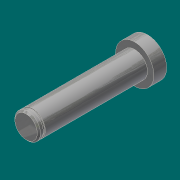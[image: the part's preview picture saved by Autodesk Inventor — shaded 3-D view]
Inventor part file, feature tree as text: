
AUTODESK INVENTOR PART (.ipt)
format: ipt  version: 2017 (Build 210142000, 142)  size: 109,568 bytes
history: native  units: in
note: dims shown in document units (in); Inventor stores cm internally (conversion verified against a paired STEP export)
features: extrude x5, sketch x5, chamfer x1
ambient origin geometry x8: Origin, YZ Plane, XZ Plane, XY Plane, X Axis, Y Axis, Z Axis, Center Point
bodies: Solid1 (feature_tree)
feature tree (11):
  extrude  "Extrusion1"  Depth=0.25in TaperAngle=0.0deg
  extrude  "Extrusion2"  Depth=2.0in TaperAngle=0.0deg
  extrude  "Extrusion3"  Depth=0.04in TaperAngle=0.0deg
  extrude  "Extrusion4"  Depth=0.125in TaperAngle=45.0deg
  chamfer  "Chamfer1"  Distance=0.125in
  extrude  "Extrusion5"  [1 undecoded]
  sketch  "Sketch1"  dims[d0=0.75in d1=0.25in d2=0.0in]
  sketch  "Sketch2"  dims[d3=0.5in d4=2.0in d5=0.0in]
  sketch  "Sketch3"  dims[d6=0.4688in d7=0.04in d8=0.0in]
  sketch  "Sketch4"  dims[d9=0.085in d10=0.0in d11=0.0312in d12=0.125in d13=45.0deg]
  sketch  "Sketch5"  dims[d14=0.25in d15=0.125in d16=0.0in]
note: 1 required parameter value undecoded (feature->parameter linkage not recoverable at this tier; creation-order binding heuristic only, values carry confidence <= 0.55)
